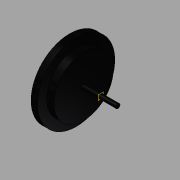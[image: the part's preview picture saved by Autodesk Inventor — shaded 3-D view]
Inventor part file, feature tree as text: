
AUTODESK INVENTOR PART (.ipt)
format: ipt  version: 2015 (Build 190159000, 159)  size: 138,752 bytes
history: native  units: in
note: dims shown in document units (in); Inventor stores cm internally (conversion verified against a paired STEP export)
features: sketch x5, other x3, plane x1
ambient origin geometry x8: Origin, YZ Plane, XZ Plane, XY Plane, X Axis, Y Axis, Z Axis, Center Point
bodies: Solid1 (feature_tree)
feature tree (9):
  other  "rueda.ipt"
  other  "Solid1::rueda.ipt"
  other  "TaggingFeature1"
  sketch  "Sketch2"  dims[d0=0.3937in]
  sketch  "Sketch3"
  sketch  "Sketch7"
  sketch  "Sketch12"
  sketch  "Sketch13"
  plane  "Work Plane1"
